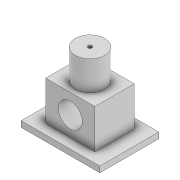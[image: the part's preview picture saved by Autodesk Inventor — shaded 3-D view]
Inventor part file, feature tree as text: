
AUTODESK INVENTOR PART (.ipt)
format: ipt  version: 2022 (Build 260153000, 153)  size: 127,488 bytes
history: native  units: mm
features: extrude x4, sketch x4, projected_geometry x1
ambient origin geometry x8: Origin, YZ Plane, XZ Plane, XY Plane, X Axis, Y Axis, Z Axis, Center Point
bodies: Solid1 (feature_tree)
feature tree (9):
  extrude  "Extrusion1"  Depth=25.0mm
  extrude  "Extrusion2"  Depth=20.0mm TaperAngle=0.0deg
  extrude  "Extrusion3"  Depth=100.0mm TaperAngle=0.0deg
  extrude  "Extrusion4"  Depth=15.0mm TaperAngle=0.0deg
  sketch  "Sketch1"  dims[d0=12.2mm d1=25.0mm]
  sketch  "Sketch2"  dims[d2=20.0mm d3=20.0mm d4=0.0mm]
  sketch  "Sketch3"  dims[d5=2.0mm d6=100.0mm d7=0.0mm]
  projected_geometry  "Projected Loop1"
  sketch  "Sketch4"  dims[d8=15.0mm d9=15.0mm d10=0.0mm d11=30.0mm d12=40.0mm d13=3.0mm d14=0.0mm]
